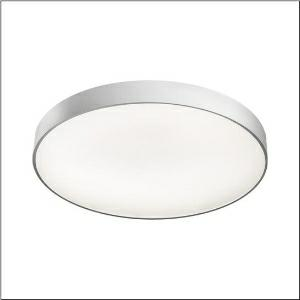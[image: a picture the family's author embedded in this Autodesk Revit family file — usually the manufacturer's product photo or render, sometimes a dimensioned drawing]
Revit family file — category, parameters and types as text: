
# Revit family: round_21_l_51mr38nd0421s
name_source: partatom
category: Lighting Fixtures
units: mm (PartAtom-declared; Revit-internal decimal feet)

## family parameters
Cut with Voids When Loaded = No
Host = Face
Light Source = No
Part Type = Normal
Room Calculation Point = No
Round Connector Dimension = Use Diameter
Shared = No

## types (1)
- Round 21 L (1 x LED, 12230 lm, 88.2 W, 4000K)
    Apparent Load = 88 VA
    CIE Flux Codes = 66 90 98 71 100
    Color Rendering = 80
    Color Temperature = 4000K
    Default Elevation = 1800 mm
    Description = Round 21 L, wall and ceiling luminaire, primary optical cover: micro prismatic cover, of PMMA, transparent, CAT 2 (L<= 3000cd/m²), light emission: direct/indirect distribution, primary light characteristic: symmetric, installation type: suspended mounting, surface-mounted, LED, rated luminous flux: 12.230lm, luminous efficacy: 139lm/W, light colour: 840, colour temperature: 4000K, control gear: DALI 2, with terminal, 5-pole, mains connection: 230V, AC, 50/60Hz, rated input power: 88W, housing, of aluminium, coated, silver, diameter: 850mm, height: 62mm, protection rating (complete): IP40, insulation class (complete): insulation class I (protective earthing), certification: CE, impact resistance: IK04, permissible operating ambient temperature: -10..+35°C, packaging unit: 1 piece
    Height = 87 mm
    Lamp = 1 x LED
    Lamp Light Flux = 12230 lm
    Lamp Power = 88.2 W
    Lamp count = 1
    Length = 850 mm
    Luminous efficacy = 139 lm/W
    Manufacturer = Siteco
    ModVariant = No
    Model = 51MR38ND0421S
    Mounting Place = Ceiling
    Mounting Type = Surface mounted
    Number of Poles = 1
    OnlyDefault = Yes
    Power Factor = 1
    Product Name = Round 21 L
    Product group = wall and ceiling luminaire
    ProductGroupID = 304
    Protection Class = Protection class I
    Protection Degree = IP 40
    RLX_Detail_Level = 1
    RLX_Emergency_Light_Flux = 0 lm
    RLX_Emergency_Type = 0
    RLX_Emergency_Type_DB = No
    RlxData = <blob elided: 25169 chars, md5=4ccf7118>
    Socket = socket
    Standby Power = 0 W
    System Light Flux = 12230 lm
    System Power = 88 W
    Type Comments = Product without accessories
    Type Image = l_1258322.jpg
    URL = http://relux.com
    VarID = ---
    Voltage = 0 V
    Weight = 0.00 kg
    Width = 0 mm  [stored 0 ft]

note: [stored X ft] marks values corroborated as IEEE doubles in the binary element streams (Revit-internal decimal feet)

## geometry (parser evidence)
native form markers: Blend x4, Sweep x13
no freeform markers — native parametric forms only
